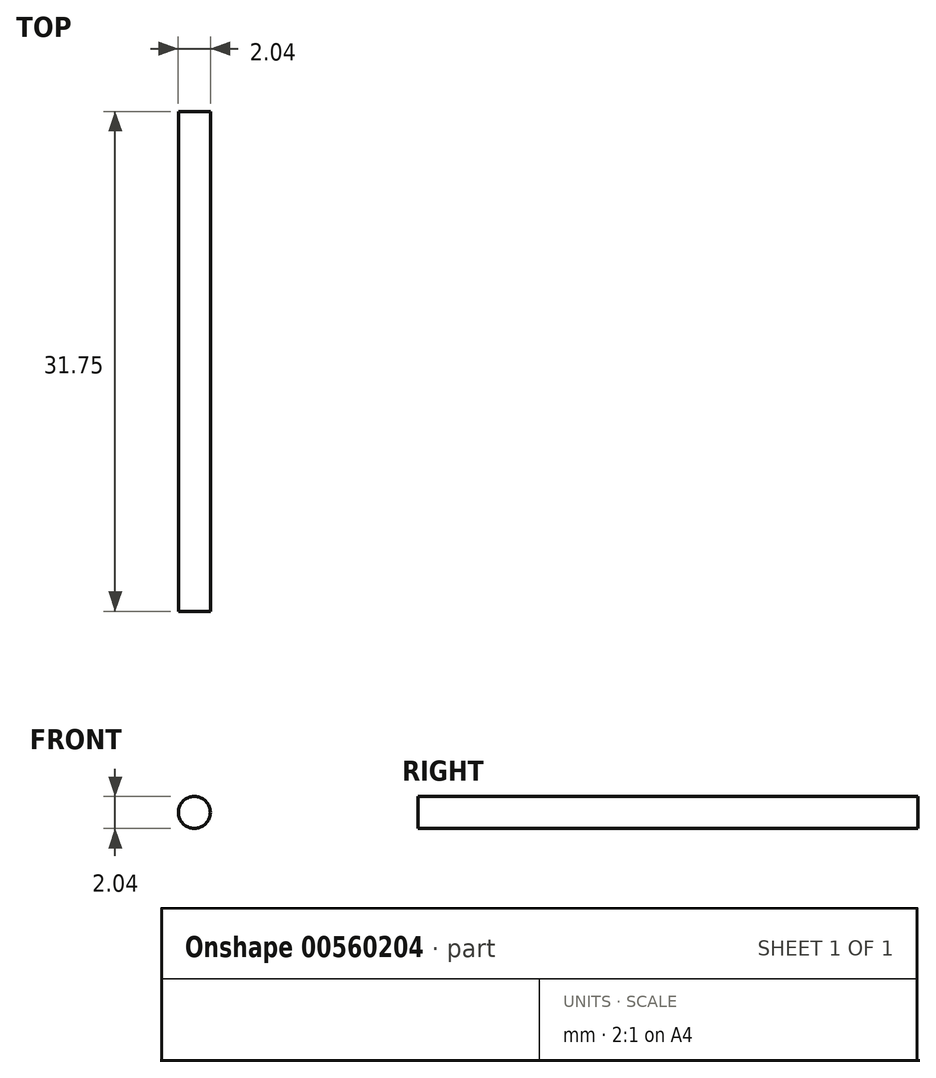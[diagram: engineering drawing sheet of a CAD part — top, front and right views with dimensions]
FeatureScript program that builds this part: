
annotation { "Feature Type Name" : "Feature", "Feature Type Description" : "" }
export const myFeature = defineFeature(function(context is Context, id is Id, definition is map)
    precondition{}
    {
        {
            var Q0;
            Q0=qCreatedBy(makeId("Front.planeOp"),FACE);
            var sketch = newSketch(context, id + "F0", { "sketchPlane" : qUnion([Q0])});
            skCircle(sketch, "E0", {"center": v(0, 0) * mm, "radius": 1.02 * mm});
            skSolve(sketch);
        }
        {
            var Q0;
            Q0 = qSketchRegion(id + "F0", true);
            extrude(context, id + "F1", {"entities" : qUnion([Q0]), "depth" : 31.75 * mm, "offsetDistance" : 25.4 * mm});
        }
    });
